# Revit family: Fireplace_Gas_Heatilator_Corner
name_source: partatom
category: Mechanical Equipment
revit_build: Autodesk Revit 2015 (Build: 20140323_1530(x64)
units: mm (PartAtom-declared; Revit-internal decimal feet)

## types (2) — shared parameters
Assembly Code = D3020
Construction Details = http://www.arcat.com
Default Elevation = 0' - 0"
Efficiency Ratings = Steady State 72  ;  AFUE 59  ;  EnerGuide 61
Electrical_Voltage = 120 V
Fixture Finish = Metal - Heatilator - Metallic Black
Fuel Consumption = as Specified
Fuel Type = NG
HVAC_BTU Input = 34000.0 Btu/h
HVAC_BTU Output = 0.0 Btu/h
Heating Capacity = as Specified
Keynote = 10305
Manufacturer = Heatilator
Manufacturer Website = http://www.heatilator.com
Opening Height = 2' - 0 1/8"
Opening Width = 3' - 0"
Product Data = http://www.arcat.com
Revision = R2_2014-09
Sales Information = http://www.heatilator.com
Send Message = http://www.arcat.com
Specification = http://www.arcat.com
Standards Conformance = UL  ;  cUL
URL = http://www.heatilator.com
Unit Depth = 2' - 0 1/2"
Unit Height = 3' - 2"
Unit Weight = 220
Unit Width = 3' - 6 1/2"
zero-valued in all types: Expected Lifespan (Years), Maintenance Schedule (Months), Warranty Duration (Years)

## per-type parameters (varying)
| type | Description | Model |
| GDCR4136 NG | Heatilator Gas Burning Fireplace - Corner GDCR4136 NG as Specified | GDCR4136 |
| GDCL4136 NG | Heatilator Gas Burning Fireplace - Corner GDCL4136 NG as Specified | GDCL4136 |

## geometry (parser evidence)
native form markers: Blend x12, Sweep x6
no freeform markers — native parametric forms only
